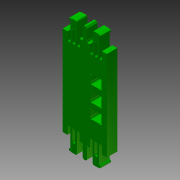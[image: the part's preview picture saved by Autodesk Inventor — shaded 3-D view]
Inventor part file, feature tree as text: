
AUTODESK INVENTOR PART (.ipt)
format: ipt  version: 2012 SP1 (Build 160190100, 190)  size: 246,272 bytes
history: native  units: in
note: dims shown in document units (in); Inventor stores cm internally (conversion verified against a paired STEP export)
features: other x3, extrude x1
ambient origin geometry x8: Origin, YZ Plane, XZ Plane, XY Plane, X Axis, Y Axis, Z Axis, Center Point
bodies: Solid1 (feature_tree)
feature tree (4):
  other  "skeleton.ipt"
  other  "STOCK_12MM"
  extrude  "Extrusion1"  Depth=0.3937in
  other  "THROUGH-CUT"
